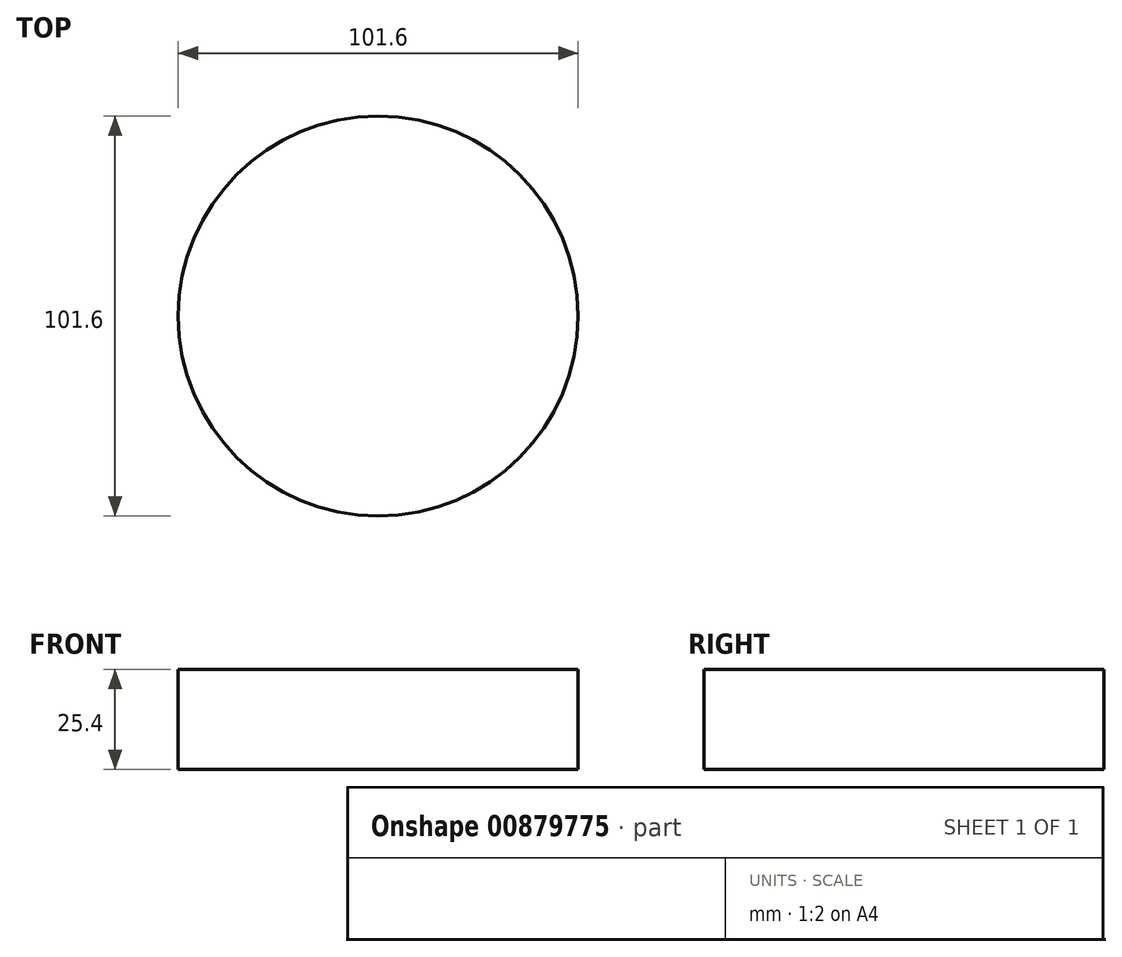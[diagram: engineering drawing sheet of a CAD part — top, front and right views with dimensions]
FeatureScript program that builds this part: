
annotation { "Feature Type Name" : "Feature", "Feature Type Description" : "" }
export const myFeature = defineFeature(function(context is Context, id is Id, definition is map)
    precondition{}
    {
        {
            var Q0;
            Q0=qCreatedBy(makeId("Top.planeOp"),FACE);
            var sketch = newSketch(context, id + "F0", { "sketchPlane" : qUnion([Q0])});
            skCircle(sketch, "E0", {"center": v(0, 0) * mm, "radius": 50.8 * mm});
            skSolve(sketch);
        }
        {
            var Q0;
            Q0 = qSketchRegion(id + "F0", true);
            extrude(context, id + "F1", {"entities" : qUnion([Q0]), "depth" : 25.4 * mm, "offsetDistance" : 25.4 * mm});
        }
    });
